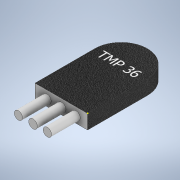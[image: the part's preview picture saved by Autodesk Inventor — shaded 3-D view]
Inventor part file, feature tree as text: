
AUTODESK INVENTOR PART (.ipt)
format: ipt  version: 2021 (Build 250183000, 183)  size: 126,464 bytes
history: native  units: mm
features: sketch x3, extrude x2, fillet x1
ambient origin geometry x8: Origin, YZ Plane, XZ Plane, XY Plane, X Axis, Y Axis, Z Axis, Center Point
bodies: Solid1 (feature_tree)
feature tree (6):
  extrude  "Extrusion1"  Depth=55.0mm
  fillet  "Fillet1"  Radius=15.0mm
  extrude  "Extrusion2"  [1 undecoded]
  sketch  "Sketch3"
  sketch  "Sketch1"  dims[d0=90.0mm d1=55.0mm d2=15.0mm d3=0.0mm]
  sketch  "Sketch2"  dims[d4=30.0mm d5=0.0mm]
note: 1 required parameter value undecoded (feature->parameter linkage not recoverable at this tier; creation-order binding heuristic only, values carry confidence <= 0.55)
